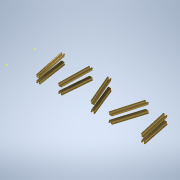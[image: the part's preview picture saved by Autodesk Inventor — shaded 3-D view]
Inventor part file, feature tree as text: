
AUTODESK INVENTOR PART (.ipt)
format: ipt  version: 2022 (Build 260153000, 153)  size: 729,088 bytes
history: native  units: mm
features: sketch x28, loft x10, plane x1
ambient origin geometry x8: Origin, YZ Plane, XZ Plane, XY Plane, X Axis, Y Axis, Z Axis, Center Point
bodies: Body1 (feature_tree)
feature tree (39):
  sketch  "Sketch3"  dims[d29=150.0mm d35=2.0mm]
  sketch  "Sketch4"  dims[d36=90.0deg d37=2.0mm]
  sketch  "Sketch5"  dims[d38=90.0deg d43=2.0mm]
  sketch  "Sketch6"  dims[d44=2.0mm d51=2.0mm]
  plane  "Work Plane2"
  sketch  "Sketch9"  dims[d52=2.0mm d56=2.0mm]
  sketch  "Sketch10"  dims[d57=2.0mm d65=2.0mm]
  sketch  "Sketch14"  dims[d66=2.0mm d69=2.0mm]
  sketch  "Sketch15"  dims[d70=2.0mm d76=2.0mm]
  sketch  "Sketch16"  dims[d77=0.0mm d150=1.8mm]
  sketch  "Sketch17"  dims[d151=1.8mm d156=1.8mm]
  sketch  "Sketch18"  dims[d157=1.8mm]
  sketch  "Sketch19"  dims[d167=1.8mm]
  sketch  "Sketch20"  dims[d168=90.0deg]
  sketch  "Sketch21"  dims[d169=1.8mm]
  sketch  "Sketch22"  dims[d170=90.0deg]
  sketch  "Sketch23"  dims[d175=1.8mm]
  sketch  "Sketch24"  dims[d176=1.8mm]
  sketch  "Sketch25"  dims[d187=1.8mm]
  sketch  "Sketch26"  dims[d188=1.8mm]
  sketch  "Sketch27"  dims[d193=1.8mm]
  sketch  "Sketch28"  dims[d194=90.0deg]
  sketch  "Sketch29"  dims[d195=1.8mm]
  sketch  "Sketch30"  dims[d196=90.0deg]
  sketch  "Sketch31"  dims[d203=25.0mm]
  sketch  "Sketch32"  dims[d204=25.0mm]
  sketch  "Sketch33"  dims[d205=25.0mm d206=25.0mm]
  sketch  "Sketch34"  dims[d207=25.0mm d208=25.0mm]
  sketch  "Sketch35"  dims[d209=25.0mm d210=25.0mm d211=25.0mm d212=25.0mm d213=25.0mm d214=25.0mm d215=25.0mm d216=25.0mm d217=25.0mm d218=25.0mm d219=25.0mm d220=25.0mm d221=25.0mm d222=25.0mm d223=25.0mm d224=25.0mm d225=25.0mm d226=25.0mm d227=25.0mm d228=25.0mm d229=25.0mm d230=25.0mm d231=25.0mm d232=25.0mm d233=25.0mm d234=25.0mm d235=25.0mm d236=25.0mm d237=25.0mm d238=25.0mm d239=25.0mm d240=25.0mm d241=25.0mm d242=25.0mm d245=5.0mm d250=2.0mm d253=5.0mm d254=5.0mm d257=2.0mm d273=2.0mm d281=2.0mm d293=2.0mm d301=2.0mm d310=2.0mm d318=2.0mm d324=2.0mm d337=2.0mm d340=5.0mm d343=2.0mm d349=2.0mm d351=5.0mm d352=5.0mm d356=2.0mm d364=2.0mm d365=10.0mm d366=5.0mm d367=5.0mm d373=2.0mm d383=2.0mm d394=2.0mm d405=2.0mm d412=2.0mm d415=5.0mm d421=2.0mm d422=0.0mm d423=90.0deg d424=0.0mm d425=90.0deg d426=0.0mm d427=90.0deg d428=0.0mm d429=90.0deg d430=0.0mm d431=90.0deg d432=0.0mm d433=90.0deg d434=0.0mm d435=90.0deg d436=0.0mm d437=90.0deg d438=0.0mm d439=90.0deg d440=0.0mm d441=90.0deg d442=0.0mm d443=90.0deg d444=0.0mm d445=90.0deg d446=0.0mm d447=90.0deg d448=0.0mm d449=90.0deg d450=0.0mm d451=90.0deg d452=0.0mm d453=90.0deg d454=0.0mm d455=90.0deg d456=0.0mm d457=90.0deg d458=0.0mm d459=90.0deg d460=0.0mm d461=90.0deg d6=0.5mm d7=0.872665mm d8=0.5mm d9=0.872665mm]
  loft  "Loft2"
  loft  "Loft3"
  loft  "Loft4"
  loft  "Loft5"
  loft  "Loft6"
  loft  "Loft7"
  loft  "Loft8"
  loft  "Loft9"
  loft  "Loft10"
  loft  "Loft11"
